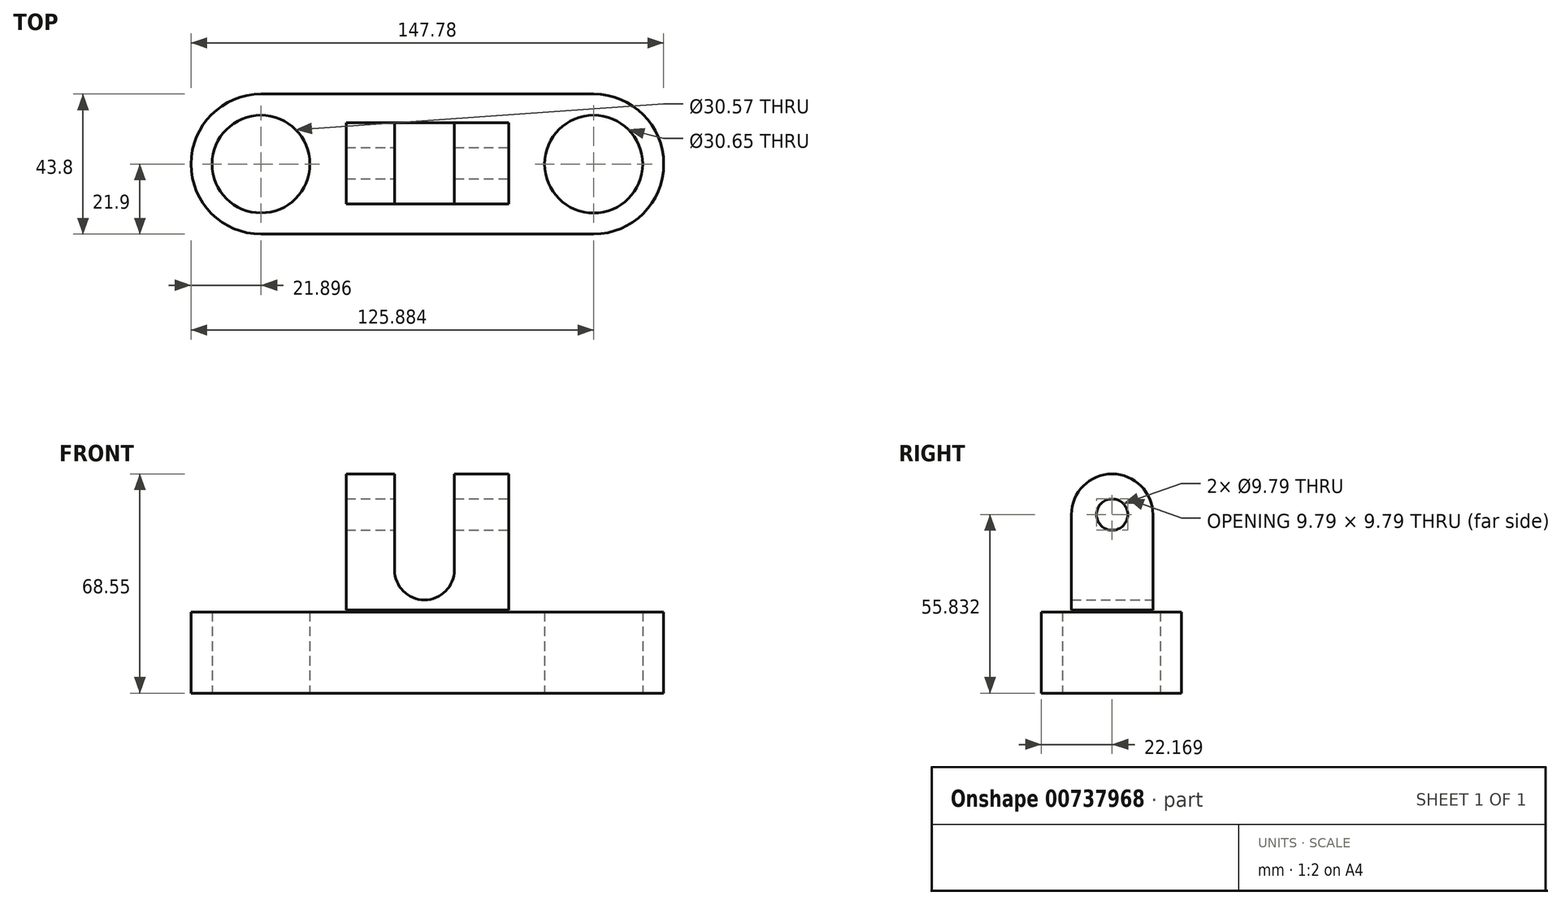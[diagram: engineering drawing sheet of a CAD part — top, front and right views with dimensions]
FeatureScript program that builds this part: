
annotation { "Feature Type Name" : "Feature", "Feature Type Description" : "" }
export const myFeature = defineFeature(function(context is Context, id is Id, definition is map)
    precondition{}
    {
        {
            var Q0;
            Q0=qCreatedBy(makeId("Top.planeOp"),FACE);
            var sketch = newSketch(context, id + "F0", { "sketchPlane" : qUnion([Q0])});
            skLineSegment(sketch, "E0.bottom", {"start": v(52, 21.9) * mm, "end": v(-52, 21.9) * mm});
            skLineSegment(sketch, "E0.top", {"start": v(52, -21.9) * mm, "end": v(-52, -21.9) * mm});
            skPoint(sketch, "E0.middle", {"position": v(0, 0) * mm});
            skArc(sketch, "E1", {"start": v(-52, 21.9) * mm, "mid": v(-73.9, 0) * mm, "end": v(-52, -21.9) * mm});
            skArc(sketch, "E2", {"start": v(52, -21.9) * mm, "mid": v(73.9, 0) * mm, "end": v(52, 21.9) * mm});
            skCircle(sketch, "E3", {"center": v(-52, 0) * mm, "radius": 15.28 * mm});
            skCircle(sketch, "E4", {"center": v(52, 0) * mm, "radius": 15.32 * mm});
            skSolve(sketch);
        }
        {
            var Q0;
            Q0=makeQuery(id+"F0.imprint","IMPRINT",FACE,{"disambiguationData":[TD([[makeQuery(id+"F0.imprint","IMPRINT",EDGE,{"derivedFrom":sQuery(id+"F0.wireOp",EDGE,"E0.bottom")}),1.0]])]});
            extrude(context, id + "F1", {"entities" : qUnion([Q0]), "depth" : 25.4 * mm, "offsetDistance" : 25.4 * mm});
        }
        {
            var Q0;
            Q0=qCreatedBy(makeId("Right.planeOp"),FACE);
            var sketch = newSketch(context, id + "F2", { "sketchPlane" : qUnion([Q0])});
            skLineSegment(sketch, "E5.bottom", {"start": v(-12.45, 25.92) * mm, "end": v(12.99, 25.92) * mm});
            skLineSegment(sketch, "E5.left", {"start": v(-12.45, 25.92) * mm, "end": v(-12.45, 55.83) * mm});
            skLineSegment(sketch, "E5.right", {"start": v(12.99, 25.92) * mm, "end": v(12.99, 55.83) * mm});
            skArc(sketch, "E6", {"start": v(12.99, 55.83) * mm, "mid": v(0.27, 68.55) * mm, "end": v(-12.45, 55.83) * mm});
            skSolve(sketch);
        }
        {
            var Q0;
            Q0 = qSketchRegion(id + "F2", true);
            extrude(context, id + "F3", {"entities" : qUnion([Q0]), "endBound" : BoundingType.SYMMETRIC, "oppositeDirection" : true, "depth" : 50.8 * mm, "offsetDistance" : 25.4 * mm});
        }
        {
            var Q0;
            Q0=makeQuery(id+"F3.opExtrude","CAP_FACE",FACE,{"disambiguationData":[OSD([sQuery(id+"F2.wireOp",EDGE,"E5.bottom"),sQuery(id+"F2.wireOp",EDGE,"E5.left"),sQuery(id+"F2.wireOp",EDGE,"E5.right"),sQuery(id+"F2.wireOp",EDGE,"E6")])],"isStart":true});
            var sketch = newSketch(context, id + "F4", { "sketchPlane" : qUnion([Q0])});
            skCircle(sketch, "E7", {"center": v(0.27, 55.83) * mm, "radius": 4.9 * mm});
            skSolve(sketch);
        }
        {
            var Q0;
            Q0 = qSketchRegion(id + "F4", true);
            extrude(context, id + "F5", {"entities" : qUnion([Q0]), "operationType" : NewBodyOperationType.REMOVE, "oppositeDirection" : true, "depth" : 50.8 * mm, "offsetDistance" : 25.4 * mm});
        }
        {
            var Q0;
            Q0=makeQuery(id+"F3.opExtrude","SWEPT_FACE",FACE,{"disambiguationData":[OSD([sQuery(id+"F2.wireOp",EDGE,"E5.right")])]});
            var sketch = newSketch(context, id + "F6", { "sketchPlane" : qUnion([Q0])});
            skLineSegment(sketch, "E8.top", {"start": v(-8.46, 72.26) * mm, "end": v(10.27, 72.26) * mm});
            skLineSegment(sketch, "E8.left", {"start": v(-8.46, 38.5) * mm, "end": v(-8.46, 72.26) * mm});
            skLineSegment(sketch, "E8.right", {"start": v(10.27, 38.5) * mm, "end": v(10.27, 72.26) * mm});
            skArc(sketch, "E9", {"start": v(-8.46, 38.5) * mm, "mid": v(0.9, 29.14) * mm, "end": v(10.27, 38.5) * mm});
            skSolve(sketch);
        }
        {
            var Q0;
            Q0 = qSketchRegion(id + "F6", true);
            extrude(context, id + "F7", {"entities" : qUnion([Q0]), "operationType" : NewBodyOperationType.REMOVE, "oppositeDirection" : true, "depth" : 50.8 * mm, "offsetDistance" : 25.4 * mm});
        }
    });
